# Revit family: EKF_EE_РейкаМонтажнаяДляЛитогоКорпусаUNIT_PROxima
name_source: partatom
category: Электрооборудование
units: mm (PartAtom-declared; Revit-internal decimal feet)

## family parameters
Всегда вертикально = Нет
На основе рабочей плоскости = Да
Общий = Да
При загрузке вырезать с полостями = Нет
Размер круглого соединителя = Использовать диаметр
Тип детали = Силовой щит
Точка расчета площади = Нет

## types (3) — shared parameters
ADSK_Единица измерения = шт.
ADSK_Завод-изготовитель = EKF
ADSK_Количество = 1
ADSK_Марка = Рейка монтажная для литого корпуса
ADSK_Материал = Сталь_Оцинкованная
ADSK_Обозначение = Рейка монтажная для литого корпуса
ADSK_Размер_Высота = 50 мм
ADSK_Размер_Глубина = 10 мм
b = 30 мм
t = 1.2 мм
Изготовитель = EKF
Отметка по умолчанию = 1219.2 мм
Серия номенклатуры = Unit PROxima
Степень защиты IP = -
ТВ = EKF_2
Тип установки = -
Шаг = 20 мм
ШагКв = 40 мм
zero-valued in all types: ADSK_Масса

## per-type parameters (varying)
| type | ADSK_Код изделия | ADSK_Размер_Ширина | Количество | Количество1 | Отступ | ОтступКв | Тип |
| Рейка монтажная для литого корпуса для ВРУ Unit шириной 450мм EKF PROxima | mb-15-rl-45 | 368 мм | 17 | 9 | 24 мм | 24 мм | 72 мм |
| Рейка монтажная для литого корпуса для ВРУ Unit шириной 600мм EKF PROxima | mb-15-rl-60 | 518 мм | 24 | 12 | 29 мм | 39 мм | 73 мм |
| Рейка монтажная для литого корпуса для ВРУ Unit шириной 800мм EKF PROxima | mb-15-rl-80 | 718 мм | 34 | 17 | 29 мм | 39 мм | 74 мм |

note: column(s) folded — value = type name in every type: ADSK_Наименование
